# Revit family: RN 82208 Optipress-Aquaplus-Valvola diritta
name_source: partatom
category: Rohrzubehör
units: mm (PartAtom-declared; Revit-internal decimal feet)

## family parameters
Arbeitsebenenbasiert = Nein
Beim Laden mit Abzugskörper schneiden = Nein
Bemaßung runder Anschluss = Durchmesser verwenden
Gemeinsam genutzt = Nein
Immer vertikal = Ja
Teiletyp = Ventil - Zerlegung in

## types (2) — shared parameters
1.010.00.2 Number of the part of the guideline = 17
1.010.00.3 Issue date (month) of the guideline = 201601
1.010.00.4 Manufacturer name = R. Nussbaum AG
1.010.00.5 Revision date of the file = 20190528
1.100.00.3 Sort number for display sequence = 1
1.100.00.4 Product designation = Rubinetti di chiusura
1.960/3L.00.8 Link (URL) = https://www.nussbaum.ch
17.700.00.4 valve assembly type = 1
17.700.00.7 maximum operating temperature TB [°C] = 90
17.700.00.8 maximum operating pressure(working pressure) ps [1.0 · 105 Pa] = 16
Connector Visibility = Nein
EnclosingSpace Visibility = Nein

## per-type parameters (varying)
| type | 1.800.00.3 BS number | 1.810.00.3 Manufacturer’s reference number | 1.810.00.4 DATANORM number | 1.810.00.5 StLB number | 1.810.00.6 GTIN number | 17.700.00.30 product description | 17.700.00.5 nominal size DN | 17.700.00.6 kvs-value [m3/h] | CONNECTOR0_DIAMETER_dX_0r | CONNECTOR0_dX_00 | CONNECTOR0_dX_01 | CONNECTOR0_ref_dX | CONNECTOR1_DIAMETER_dX_0r | CONNECTOR1_dX_00 | CONNECTOR1_dX_01 | CONNECTOR1_ref_dX | R. Nussbaum AG 82208.24 it Visibility | R. Nussbaum AG 82208.25 it Visibility |
| DN 20 | 0010970000000000000000000000020070000000000000000100000000 | 82208.24 | 82208.24 | 623.464 | 7612945733016 | 82208.24, Optipress-Aquaplus-Valvola diritta, uscita con filetto femmina, DN=20, | 20 | 5.86 | 20 mm | 46 mm | 22 mm | 22 mm | 20 mm | 27 mm | 42 mm | 27 mm | Ja | Nein |
| DN 25 | 0010970000000000000000000000020070000000000000000200000000 | 82208.25 | 82208.25 | 623.465 | 7612945728821 | 82208.25, Optipress-Aquaplus-Valvola diritta, uscita con filetto femmina, DN=25, | 25 | 9.41 | 25 mm  [stored 0.082021 ft] | 54 mm | 30 mm | 30 mm | 25 mm  [stored 0.082021 ft] | 34 mm | 51 mm | 34 mm | Nein | Ja |

note: [stored X ft] marks values corroborated as IEEE doubles in the binary element streams (Revit-internal decimal feet)

## geometry (parser evidence)
native form markers: Sweep x3
no freeform markers — native parametric forms only
